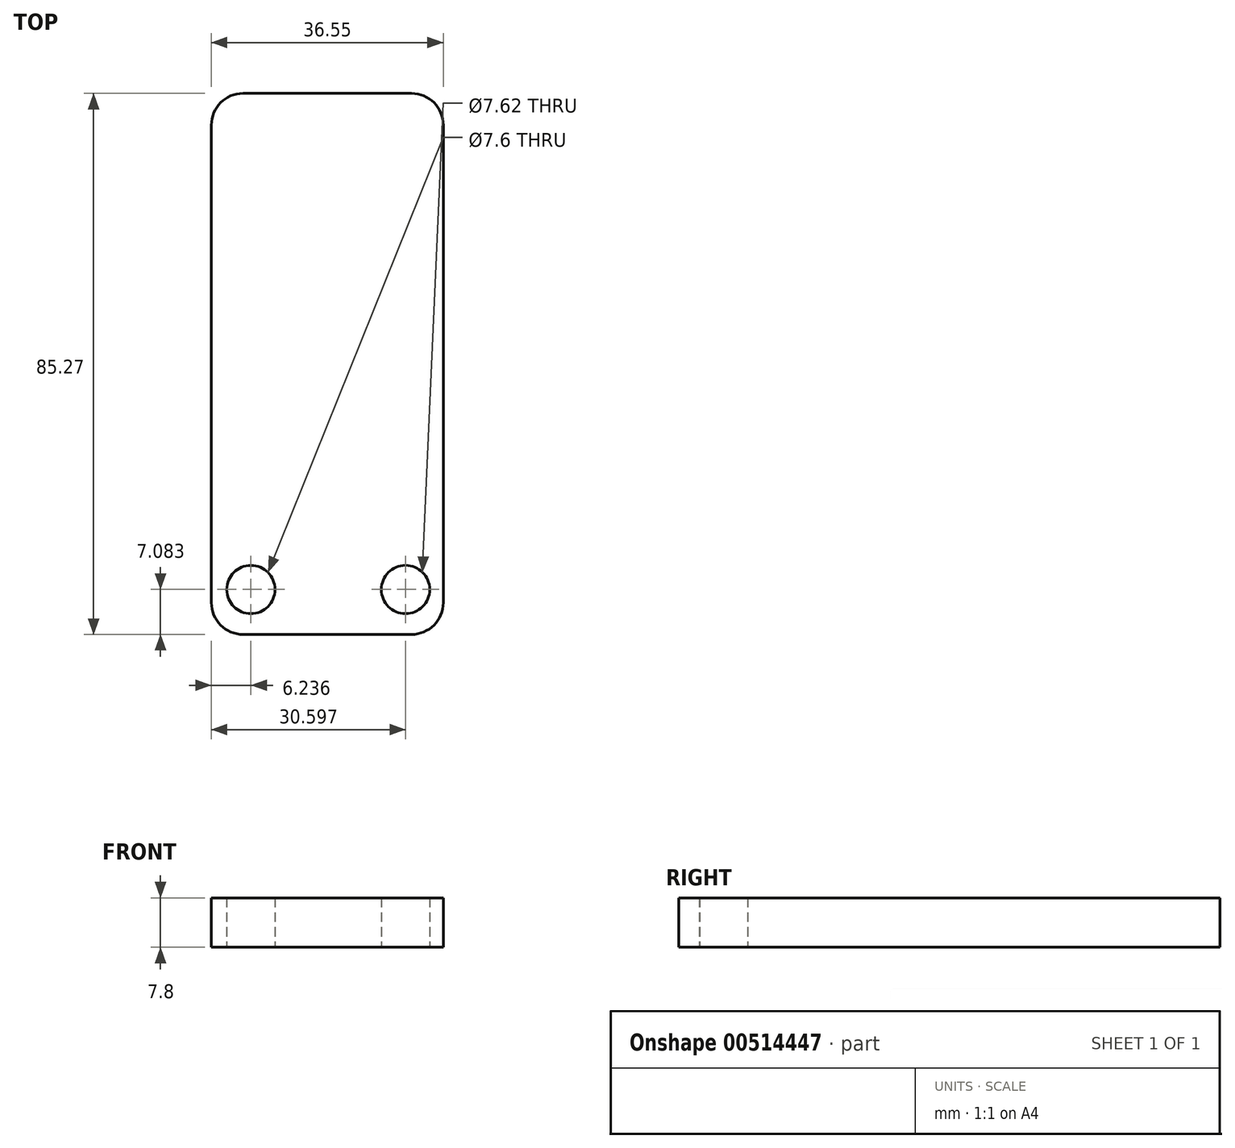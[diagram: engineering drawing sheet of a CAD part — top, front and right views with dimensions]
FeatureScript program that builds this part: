
annotation { "Feature Type Name" : "Feature", "Feature Type Description" : "" }
export const myFeature = defineFeature(function(context is Context, id is Id, definition is map)
    precondition{}
    {
        {
            var Q0;
            Q0=qCreatedBy(makeId("Top.planeOp"),FACE);
            var sketch = newSketch(context, id + "F0", { "sketchPlane" : qUnion([Q0])});
            skLineSegment(sketch, "E0.bottom", {"start": v(-17.85, 34.28) * mm, "end": v(18.7, 34.28) * mm});
            skLineSegment(sketch, "E0.top", {"start": v(-17.85, -50.99) * mm, "end": v(18.7, -50.99) * mm});
            skLineSegment(sketch, "E0.left", {"start": v(-17.85, 34.28) * mm, "end": v(-17.85, -50.99) * mm});
            skLineSegment(sketch, "E0.right", {"start": v(18.7, 34.28) * mm, "end": v(18.7, -50.99) * mm});
            skCircle(sketch, "E1", {"center": v(12.75, -43.9) * mm, "radius": 3.81 * mm});
            skCircle(sketch, "E2", {"center": v(-11.61, -43.9) * mm, "radius": 3.8 * mm});
            skSolve(sketch);
        }
        {
            var Q0;
            Q0=makeQuery(id+"F0.imprint","IMPRINT",FACE,{"disambiguationData":[TD([[makeQuery(id+"F0.imprint","IMPRINT",EDGE,{"derivedFrom":sQuery(id+"F0.wireOp",EDGE,"E0.bottom")}),-1.0]])]});
            extrude(context, id + "F1", {"entities" : qUnion([Q0]), "depth" : 7.8 * mm});
        }
        {
            var Q0;
            Q0=makeQuery(id+"F1.opExtrude","SWEPT_EDGE",EDGE,{"disambiguationData":[OSD([sQuery(id+"F0.wireOp",EDGE,"E0.top"),sQuery(id+"F0.wireOp",EDGE,"E0.left")])]});
            var Q1;
            Q1=makeQuery(id+"F1.opExtrude","SWEPT_EDGE",EDGE,{"disambiguationData":[OSD([sQuery(id+"F0.wireOp",EDGE,"E0.top"),sQuery(id+"F0.wireOp",EDGE,"E0.right")])]});
            var Q2;
            Q2=makeQuery(id+"F1.opExtrude","SWEPT_EDGE",EDGE,{"disambiguationData":[OSD([sQuery(id+"F0.wireOp",EDGE,"E0.bottom"),sQuery(id+"F0.wireOp",EDGE,"E0.right")])]});
            var Q3;
            Q3=makeQuery(id+"F1.opExtrude","SWEPT_EDGE",EDGE,{"disambiguationData":[OSD([sQuery(id+"F0.wireOp",EDGE,"E0.bottom"),sQuery(id+"F0.wireOp",EDGE,"E0.left")])]});
            fillet(context, id + "F2", {"entities" : qUnion([Q0, Q1, Q2, Q3]), "radius" : 5 * mm, "tangentPropagation" : true, "allowEdgeOverflow" : false});
        }
    });
